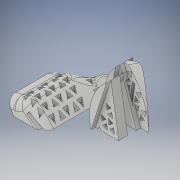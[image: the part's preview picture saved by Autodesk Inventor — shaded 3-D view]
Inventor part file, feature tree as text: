
AUTODESK INVENTOR PART (.ipt)
format: ipt  version: 2017 (Build 210142000, 142)  size: 1,657,344 bytes
history: native  units: mm
features: sketch x29, extrude x25, plane x7, fillet x6, move_body x5, other x4, boolean_combine x1, revolve x1, sweep x1, split x1
ambient origin geometry x8: Origin, YZ Plane, XZ Plane, XY Plane, X Axis, Y Axis, Z Axis, Center Point
bodies: Solid1 (feature_tree), Solid2 (feature_tree), Solid3 (feature_tree), Solid4 (feature_tree), Solid5 (feature_tree), Solid6 (feature_tree), Solid7 (feature_tree)
feature tree (80):
  extrude  "Extrusion1"  Depth=35.0mm
  plane  "Work Plane1"
  extrude  "Extrusion2"  Depth=33.005mm
  extrude  "Extrusion3"  TaperAngle=0.0deg  [1 undecoded]
  plane  "Work Plane2"
  extrude  "Extrusion4"  Depth=20.0mm
  other  "Work Axis1"
  extrude  "Extrusion5"  Depth=10.0mm
  sketch  "Sketch6"  dims[d12=48.556624mm d13=20.0mm d14=0.0mm]
  boolean_combine  "Combine1"
  extrude  "Extrusion6"  Depth=20.0mm TaperAngle=0.0deg
  extrude  "Extrusion7"  Depth=20.0mm TaperAngle=0.0deg
  other  "Work Axis2"
  fillet  "Fillet1"  Radius=53.287466mm
  revolve  "Revolution1"  [1 undecoded]
  extrude  "Extrusion8"  Depth=61.358233mm
  sketch  "Sketch10"  dims[d25=7.433428mm d26=13.25mm d27=0.0mm]
  plane  "Work Plane3"
  sweep  "Sweep1"
  extrude  "Extrusion9"  TaperAngle=90.0deg  [1 undecoded]
  fillet  "Fillet2"  Radius=40.197898mm
  extrude  "Extrusion10"  Depth=15.060899mm
  extrude  "Extrusion11"  Depth=10.650813mm
  extrude  "Extrusion12"  Depth=5.3475mm
  fillet  "Fillet3"  Radius=15.0mm
  fillet  "Fillet4"  [1 undecoded]
  fillet  "Fillet5"  Radius=27.295196mm
  other  "Bend Part1"
  extrude  "Extrusion13"  Depth=5.348mm
  plane  "Work Plane4"
  extrude  "Extrusion14"  TaperAngle=0.0deg  [1 undecoded]
  fillet  "Fillet6"  Radius=13.25mm
  extrude  "Extrusion15"  Depth=75.0mm TaperAngle=0.0deg
  plane  "Work Plane5"
  extrude  "Extrusion16"  Depth=10.0mm
  extrude  "Extrusion22"  Depth=10.0mm TaperAngle=0.0deg
  extrude  "Extrusion23"  Depth=10.0mm
  extrude  "Extrusion24"  Depth=10.0mm TaperAngle=180.0deg
  extrude  "Extrusion25"  Depth=18.153275mm
  plane  "Work Plane7"
  extrude  "Extrusion26"  TaperAngle=90.0deg  [1 undecoded]
  extrude  "Extrusion27"  Depth=75.0mm
  extrude  "Extrusion28"  Depth=75.0mm
  plane  "Work Plane8"
  extrude  "Extrusion29"  Depth=17.5mm
  split  "Split1"
  move_body  "Move Body1"
  move_body  "Move Body2"
  move_body  "Move Body3"
  move_body  "Move Body4"
  move_body  "Move Body5"
  sketch  "Sketch1"  dims[d0=60.0mm d1=35.0mm]
  sketch  "Sketch2"  dims[d2=60.0mm d3=33.005mm]
  sketch  "Sketch3"  dims[d4=75.0mm d5=0.0mm d6=0.0mm]
  sketch  "Sketch4"  dims[d7=35.0mm d8=20.0mm]
  sketch  "Sketch5"  dims[d9=55.0mm d10=0.0mm d11=10.0mm]
  sketch  "Sketch7"  dims[d15=90.0deg d16=20.0mm d17=0.0mm d18=53.287466mm]
  sketch  "Sketch8"  dims[d19=20.0mm d20=0.0mm d21=14.476257mm]
  sketch  "Sketch9"  dims[d22=20.0mm d23=0.0mm d24=61.358233mm]
  sketch  "Sketch11"  dims[d28=10.0mm d29=90.0deg d30=40.197898mm]
  sketch  "Sketch12"  dims[d31=90.965929mm d32=15.060899mm]
  sketch  "Sketch13"  dims[d33=0.0mm d34=0.0mm d35=10.650813mm]
  sketch  "Sketch15"  dims[d36=90.0deg d37=5.3475mm d38=15.0mm d39=45.0deg d40=27.295196mm]
  sketch  "Sketch16"  dims[d41=20.0mm d42=5.348mm]
  sketch  "Sketch18"  dims[d43=60.0mm d44=0.0mm d45=0.0mm d46=13.25mm d47=0.0mm]
  sketch  "Sketch19"  dims[d48=10.0mm d49=75.0mm d50=0.0mm]
  sketch  "Sketch20"  dims[d52=10.0mm d53=10.80569mm]
  sketch  "Sketch21"  dims[d54=10.0mm d55=0.0mm d56=4.8mm d57=0.0mm]
  sketch  "Sketch22"  dims[d58=10.0mm d59=10.0mm]
  sketch  "Sketch28"  dims[d60=10.0mm d62=2.0mm d63=180.0deg]
  sketch  "Sketch29"  dims[d64=18.153275mm d65=18.153275mm]
  sketch  "Sketch30"  dims[d66=75.0mm d67=0.0mm d68=90.0deg]
  sketch  "Sketch31"  dims[d69=75.0mm d70=57.396209mm]
  sketch  "Sketch32"  dims[d71=75.0mm d72=0.0mm d73=2.0mm]
  sketch  "Sketch33"  dims[d74=27.7545mm d75=17.5mm]
  sketch  "Sketch34"  dims[d76=5.0mm d77=0.0mm d78=20.0mm]
  sketch  "Sketch35"  dims[d79=28.8585mm]
  sketch  "Sketch36"  dims[d80=10.0mm d81=0.0mm d108=10.0mm d109=0.0mm d110=5.0mm d111=0.0mm d112=20.0mm d113=3.0mm d114=2.5mm d115=19.198622mm d116=10.0mm d117=0.0mm d118=20.0mm d119=3.0mm d120=13.189mm d121=20.0mm d122=3.0mm d123=11.073mm d124=10.0mm d125=5.0mm d126=0.0mm d127=0.0mm d128=5.202827mm d129=2.5mm d130=20.0mm d131=47.662mm d132=0.0mm d133=6.0mm d134=4.0mm d136=4.0mm d137=6.0mm d138=4.0mm d140=4.0mm d141=30.0mm d143=16.0mm d144=30.0mm d146=8.0mm d149=20.0mm d151=19.0mm d152=10.0mm d154=10.0mm d156=20.0mm d158=8.0mm d159=10.0mm d161=10.0mm d163=0.0mm d164=0.0mm d165=6.0mm d166=4.0mm d167=4.0mm d168=6.0mm d169=4.0mm d170=4.0mm d171=20.0mm d173=14.0mm d174=20.0mm d176=8.0mm d179=10.0mm d180=0.0mm d181=10.0mm d182=6.0mm d183=4.0mm d185=4.0mm d186=6.0mm d187=4.0mm d188=4.0mm d189=40.0mm d191=14.0mm d192=10.0mm d194=10.0mm d196=20.0mm d198=12.0mm d199=10.0mm d201=10.0mm d203=20.0mm d205=8.0mm d206=10.0mm d208=10.0mm d210=20.0mm d211=0.0mm d213=10.0mm d214=0.0mm d215=10.0mm d216=0.0mm d217=0.0mm d218=34.0mm d219=-28.75mm d220=14.5mm d221=-11.859512mm d222=0.0mm d223=-3.704mm d224=0.0mm d225=-43.275845mm]
  other  "Srf1"
  extrude  "ExtrusionSrf1"  Depth=20.0mm
note: 6 required parameter values undecoded (feature->parameter linkage not recoverable at this tier; creation-order binding heuristic only, values carry confidence <= 0.55)